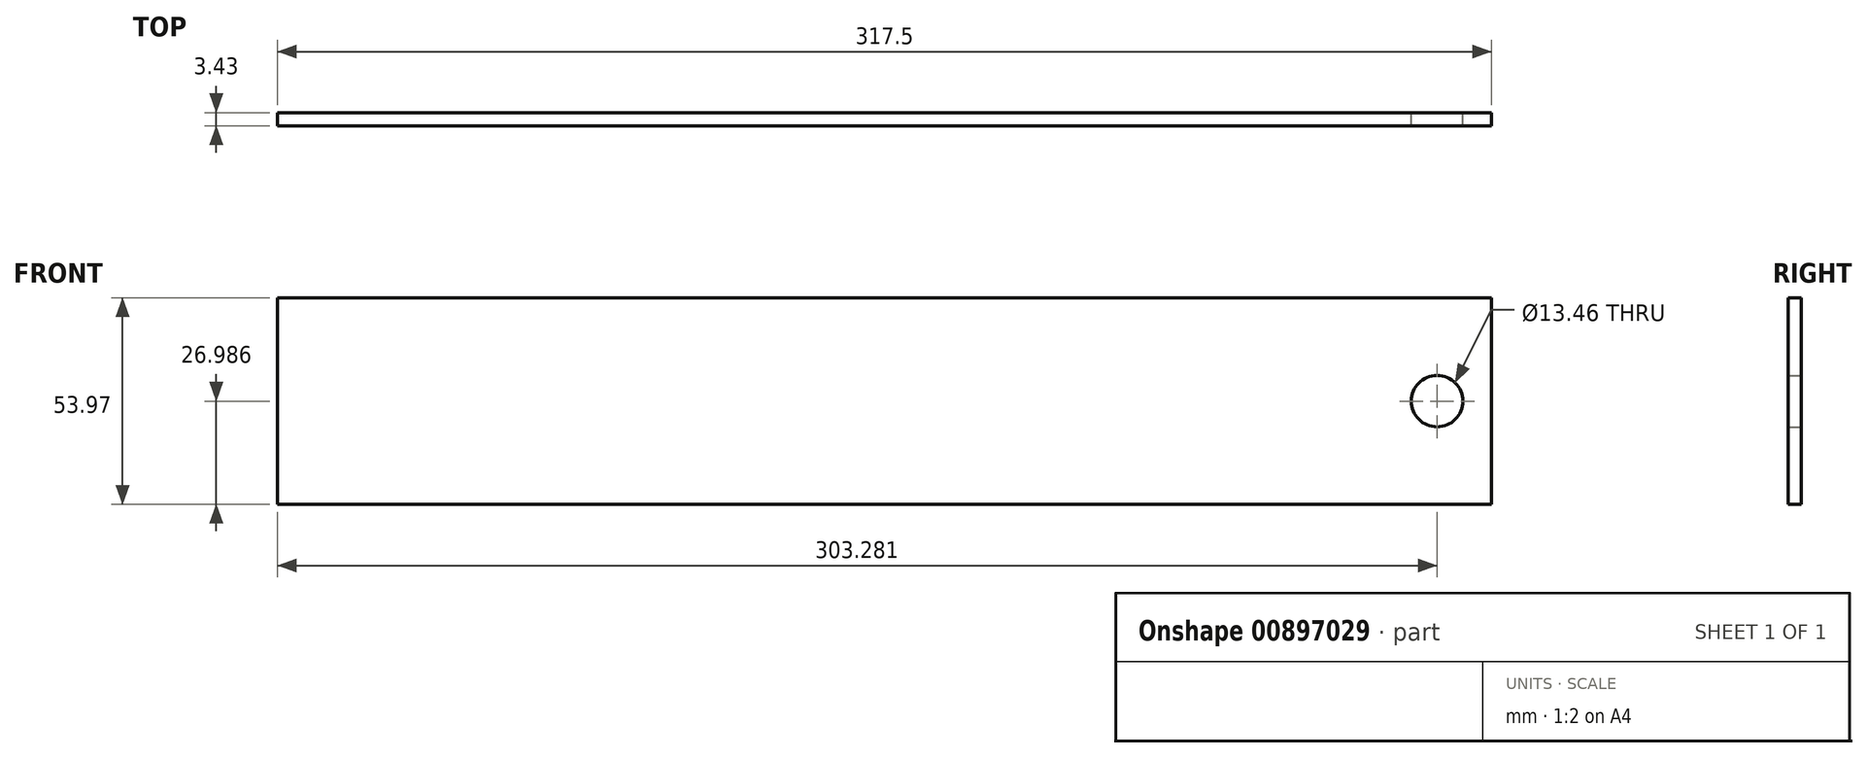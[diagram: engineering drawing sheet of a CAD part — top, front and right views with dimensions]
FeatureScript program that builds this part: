
annotation { "Feature Type Name" : "Feature", "Feature Type Description" : "" }
export const myFeature = defineFeature(function(context is Context, id is Id, definition is map)
    precondition{}
    {
        {
            var Q0;
            Q0=qCreatedBy(makeId("Front.planeOp"),FACE);
            var sketch = newSketch(context, id + "F0", { "sketchPlane" : qUnion([Q0])});
            skCircle(sketch, "E0", {"center": v(871.25, 322.5) * mm, "radius": 6.73 * mm});
            skLineSegment(sketch, "E1", {"start": v(567.97, 295.52) * mm, "end": v(885.47, 295.52) * mm});
            skLineSegment(sketch, "E2", {"start": v(567.97, 349.5) * mm, "end": v(567.97, 295.52) * mm});
            skLineSegment(sketch, "E3", {"start": v(885.47, 349.5) * mm, "end": v(567.97, 349.5) * mm});
            skLineSegment(sketch, "E4", {"start": v(885.47, 295.52) * mm, "end": v(885.47, 349.5) * mm});
            skSolve(sketch);
        }
        {
            var Q0;
            Q0 = qSketchRegion(id + "F0", true);
            extrude(context, id + "F1", {"entities" : qUnion([Q0]), "depth" : 3.43 * mm, "offsetDistance" : 25.4 * mm});
        }
    });
